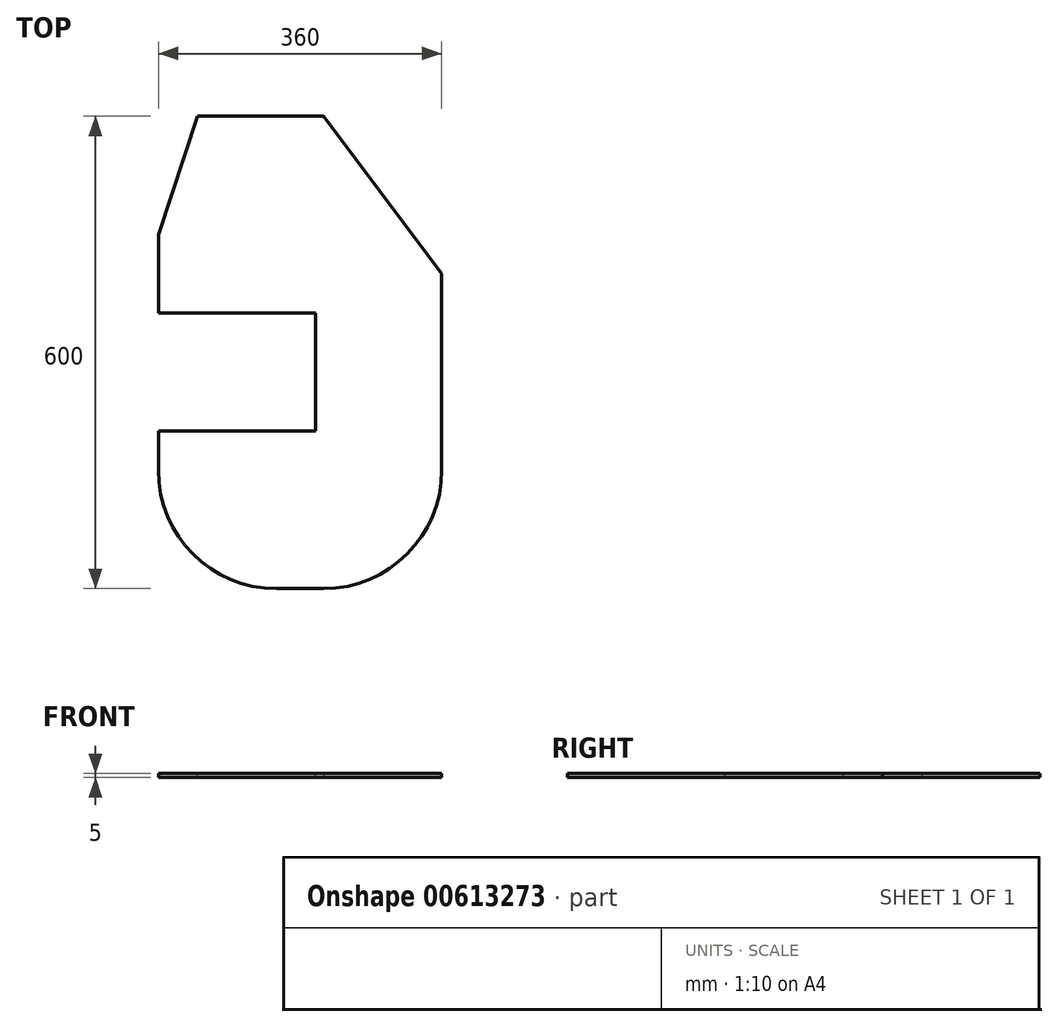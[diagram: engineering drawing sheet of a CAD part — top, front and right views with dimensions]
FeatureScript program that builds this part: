
annotation { "Feature Type Name" : "Feature", "Feature Type Description" : "" }
export const myFeature = defineFeature(function(context is Context, id is Id, definition is map)
    precondition{}
    {
        {
            var Q0;
            Q0=qCreatedBy(makeId("Top.planeOp"),FACE);
            var sketch = newSketch(context, id + "F0", { "sketchPlane" : qUnion([Q0])});
            skLineSegment(sketch, "E0.bottom", {"start": v(0, 0) * mm, "end": v(360, 0) * mm});
            skLineSegment(sketch, "E0.top", {"start": v(0, 600) * mm, "end": v(360, 600) * mm});
            skLineSegment(sketch, "E0.left", {"start": v(0, 0) * mm, "end": v(0, 600) * mm});
            skLineSegment(sketch, "E0.right", {"start": v(360, 0) * mm, "end": v(360, 600) * mm});
            skSolve(sketch);
        }
        {
            var Q0;
            Q0 = qSketchRegion(id + "F0", true);
            extrude(context, id + "F1", {"entities" : qUnion([Q0]), "depth" : 5 * mm, "offsetDistance" : 25 * mm});
        }
        {
            var Q0;
            Q0=makeQuery(id+"F1.opExtrude","CAP_FACE",FACE,{"disambiguationData":[OSD([sQuery(id+"F0.wireOp",EDGE,"E0.bottom"),sQuery(id+"F0.wireOp",EDGE,"E0.top"),sQuery(id+"F0.wireOp",EDGE,"E0.left"),sQuery(id+"F0.wireOp",EDGE,"E0.right")])],"isStart":false});
            var sketch = newSketch(context, id + "F2", { "sketchPlane" : qUnion([Q0])});
            skLineSegment(sketch, "E1.bottom", {"start": v(0, 350) * mm, "end": v(200, 350) * mm});
            skLineSegment(sketch, "E1.top", {"start": v(0, 200) * mm, "end": v(200, 200) * mm});
            skLineSegment(sketch, "E1.left", {"start": v(0, 350) * mm, "end": v(0, 200) * mm});
            skLineSegment(sketch, "E1.right", {"start": v(200, 350) * mm, "end": v(200, 200) * mm});
            skSolve(sketch);
        }
        {
            var Q0;
            Q0=makeQuery(id+"F2.imprint","IMPRINT",FACE,{"disambiguationData":[TD([[makeQuery(id+"F2.imprint","IMPRINT",EDGE,{"derivedFrom":sQuery(id+"F2.wireOp",EDGE,"E1.bottom")}),-1.0]])]});
            extrude(context, id + "F3", {"entities" : qUnion([Q0]), "operationType" : NewBodyOperationType.REMOVE, "oppositeDirection" : true, "depth" : 25 * mm, "offsetDistance" : 25 * mm});
        }
        {
            var Q0;
            Q0=makeQuery(id+"F1.opExtrude","SWEPT_EDGE",EDGE,{"disambiguationData":[OSD([sQuery(id+"F0.wireOp",EDGE,"E0.bottom"),sQuery(id+"F0.wireOp",EDGE,"E0.left")])]});
            fillet(context, id + "F4", {"entities" : qUnion([Q0]), "radius" : 150 * mm, "tangentPropagation" : true, "allowEdgeOverflow" : false});
        }
        {
            var Q0;
            Q0=makeQuery(id+"F1.opExtrude","SWEPT_EDGE",EDGE,{"disambiguationData":[OSD([sQuery(id+"F0.wireOp",EDGE,"E0.top"),sQuery(id+"F0.wireOp",EDGE,"E0.left")])]});
            chamfer(context, id + "F5", {"entities" : qUnion([Q0]), "chamferType" : ChamferType.TWO_OFFSETS, "width1" : 150 * mm, "oppositeDirection" : false, "width2" : 50 * mm, "tangentPropagation" : true});
        }
        {
            var Q0;
            Q0=makeQuery(id+"F1.opExtrude","SWEPT_EDGE",EDGE,{"disambiguationData":[OSD([sQuery(id+"F0.wireOp",EDGE,"E0.top"),sQuery(id+"F0.wireOp",EDGE,"E0.right")])]});
            chamfer(context, id + "F6", {"entities" : qUnion([Q0]), "chamferType" : ChamferType.TWO_OFFSETS, "width1" : 150 * mm, "oppositeDirection" : false, "width2" : 200 * mm, "tangentPropagation" : true});
        }
        {
            var Q0;
            Q0=makeQuery(id+"F1.opExtrude","SWEPT_EDGE",EDGE,{"disambiguationData":[OSD([sQuery(id+"F0.wireOp",EDGE,"E0.bottom"),sQuery(id+"F0.wireOp",EDGE,"E0.right")])]});
            fillet(context, id + "F7", {"entities" : qUnion([Q0]), "radius" : 150 * mm, "tangentPropagation" : true, "allowEdgeOverflow" : false});
        }
    });
